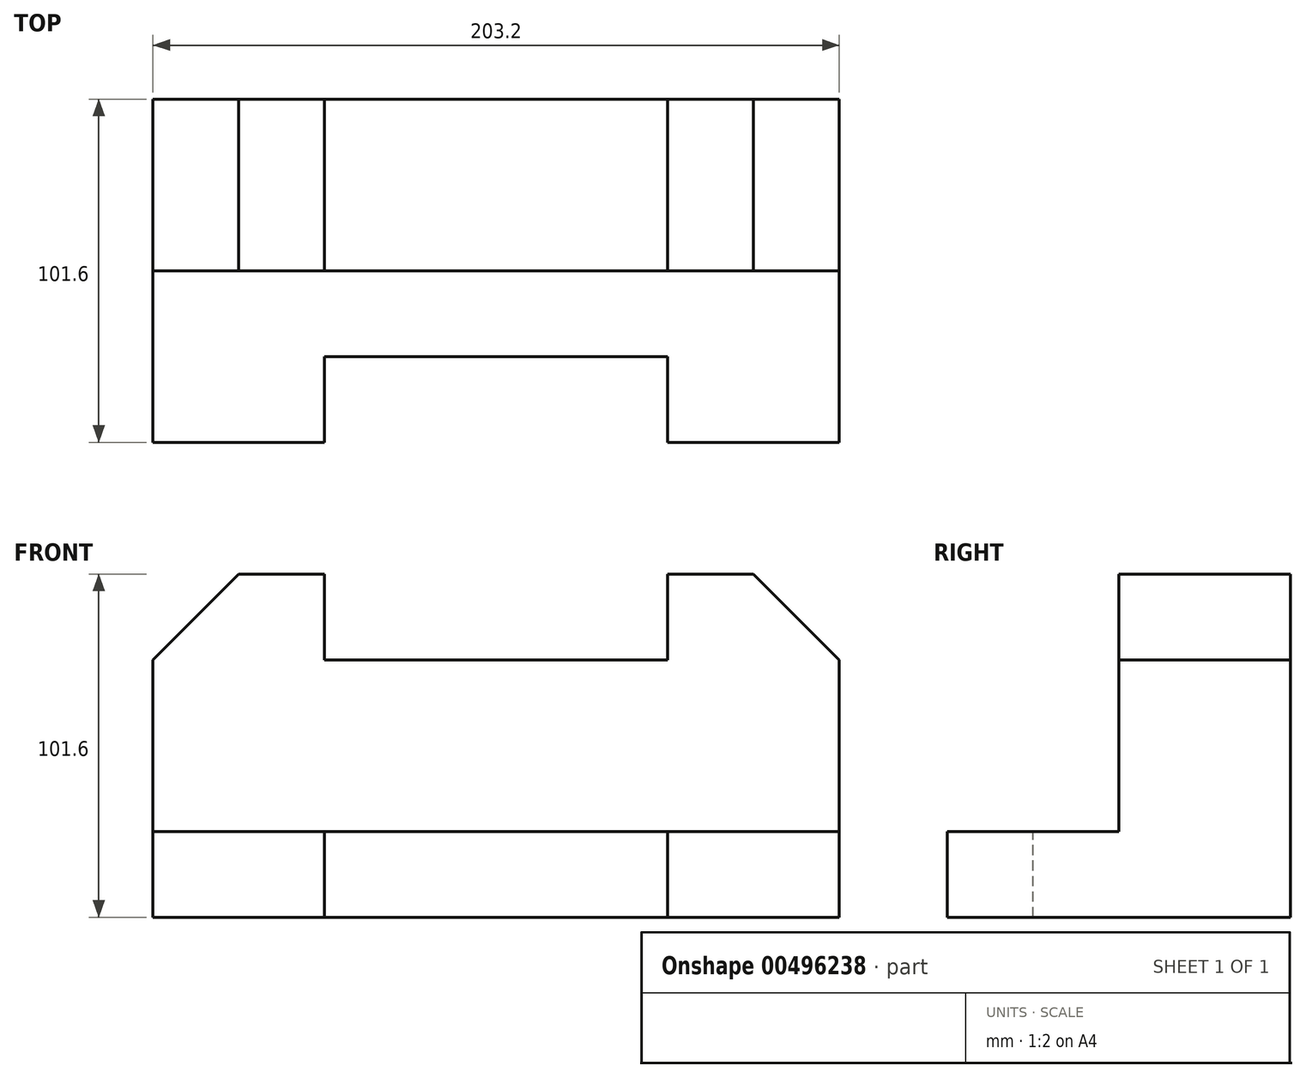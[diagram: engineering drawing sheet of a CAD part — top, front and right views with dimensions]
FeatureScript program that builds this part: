
annotation { "Feature Type Name" : "Feature", "Feature Type Description" : "" }
export const myFeature = defineFeature(function(context is Context, id is Id, definition is map)
    precondition{}
    {
        {
            var Q0;
            Q0=qCreatedBy(makeId("Front.planeOp"),FACE);
            var sketch = newSketch(context, id + "F0", { "sketchPlane" : qUnion([Q0])});
            skLineSegment(sketch, "E0.bottom", {"start": v(0, 0) * mm, "end": v(-50.8, 0) * mm});
            skLineSegment(sketch, "E0.top", {"start": v(0, 101.6) * mm, "end": v(-50.8, 101.6) * mm});
            skLineSegment(sketch, "E0.left", {"start": v(0, 0) * mm, "end": v(0, 101.6) * mm});
            skLineSegment(sketch, "E0.right", {"start": v(-50.8, 0) * mm, "end": v(-50.8, 101.6) * mm});
            skLineSegment(sketch, "E1.bottom", {"start": v(0, 0) * mm, "end": v(50.8, 0) * mm});
            skLineSegment(sketch, "E1.top", {"start": v(0, 25.4) * mm, "end": v(50.8, 25.4) * mm});
            skLineSegment(sketch, "E1.left", {"start": v(0, 0) * mm, "end": v(0, 25.4) * mm});
            skLineSegment(sketch, "E1.right", {"start": v(50.8, 0) * mm, "end": v(50.8, 25.4) * mm});
            skSolve(sketch);
        }
        {
            var Q0;
            Q0=makeQuery(id+"F0.imprint","IMPRINT",FACE,{"disambiguationData":[TD([[makeQuery(id+"F0.imprint","IMPRINT",EDGE,{"derivedFrom":sQuery(id+"F0.wireOp",EDGE,"E0.bottom")}),-1.0]])]});
            var Q1;
            Q1=makeQuery(id+"F0.imprint","IMPRINT",FACE,{"disambiguationData":[TD([[makeQuery(id+"F0.imprint","IMPRINT",EDGE,{"derivedFrom":sQuery(id+"F0.wireOp",EDGE,"E1.bottom")}),1.0]])]});
            extrude(context, id + "F1", {"entities" : qUnion([Q0, Q1]), "depth" : 203.2 * mm});
        }
        {
            var Q0;
            Q0=makeQuery(id+"F1.opExtrude","SWEPT_FACE",FACE,{"disambiguationData":[OSD([sQuery(id+"F0.wireOp",EDGE,"E1.right")])]});
            var sketch = newSketch(context, id + "F2", { "sketchPlane" : qUnion([Q0])});
            skLineSegment(sketch, "E2", {"start": v(-203.2, 0) * mm, "end": v(-152.4, 0) * mm});
            skLineSegment(sketch, "E3.bottom", {"start": v(-152.4, 0) * mm, "end": v(-50.8, 0) * mm});
            skLineSegment(sketch, "E3.top", {"start": v(-152.4, 25.4) * mm, "end": v(-50.8, 25.4) * mm});
            skLineSegment(sketch, "E3.left", {"start": v(-152.4, 0) * mm, "end": v(-152.4, 25.4) * mm});
            skLineSegment(sketch, "E3.right", {"start": v(-50.8, 0) * mm, "end": v(-50.8, 25.4) * mm});
            skSolve(sketch);
        }
        {
            var Q0;
            Q0=makeQuery(id+"F2.imprint","IMPRINT",FACE,{"disambiguationData":[TD([[makeQuery(id+"F2.imprint","IMPRINT",EDGE,{"derivedFrom":sQuery(id+"F2.wireOp",EDGE,"E3.bottom")}),1.0]])]});
            extrude(context, id + "F3", {"entities" : qUnion([Q0]), "operationType" : NewBodyOperationType.REMOVE, "oppositeDirection" : true, "depth" : 25.4 * mm});
        }
        {
            var Q0;
            Q0=makeQuery(id+"F1.opExtrude","SWEPT_FACE",FACE,{"disambiguationData":[OSD([sQuery(id+"F0.wireOp",EDGE,"E0.right")])]});
            var sketch = newSketch(context, id + "F4", { "sketchPlane" : qUnion([Q0])});
            skLineSegment(sketch, "E4", {"start": v(0, 101.6) * mm, "end": v(25.4, 101.6) * mm});
            skLineSegment(sketch, "E5", {"start": v(25.4, 101.6) * mm, "end": v(50.8, 101.6) * mm});
            skLineSegment(sketch, "E6", {"start": v(203.2, 101.6) * mm, "end": v(177.8, 101.6) * mm});
            skLineSegment(sketch, "E7", {"start": v(152.4, 101.6) * mm, "end": v(177.8, 101.6) * mm});
            skLineSegment(sketch, "E8", {"start": v(25.4, 101.6) * mm, "end": v(25.4, 76.2) * mm});
            skLineSegment(sketch, "E9", {"start": v(177.8, 101.6) * mm, "end": v(177.8, 76.2) * mm});
            skLineSegment(sketch, "E10", {"start": v(0, 101.6) * mm, "end": v(0, 76.2) * mm});
            skLineSegment(sketch, "E11", {"start": v(0, 76.2) * mm, "end": v(25.4, 101.6) * mm});
            skLineSegment(sketch, "E12", {"start": v(177.8, 101.6) * mm, "end": v(203.2, 76.2) * mm});
            skLineSegment(sketch, "E13", {"start": v(203.2, 76.2) * mm, "end": v(203.2, 101.6) * mm});
            skSolve(sketch);
        }
        {
            var Q0;
            Q0=makeQuery(id+"F4.imprint","IMPRINT",FACE,{"disambiguationData":[TD([[makeQuery(id+"F4.imprint","IMPRINT",EDGE,{"derivedFrom":sQuery(id+"F4.wireOp",EDGE,"E4")}),1.0]])]});
            var Q1;
            Q1=makeQuery(id+"F4.imprint","IMPRINT",FACE,{"disambiguationData":[TD([[makeQuery(id+"F4.imprint","IMPRINT",EDGE,{"derivedFrom":sQuery(id+"F4.wireOp",EDGE,"E6")}),1.0]])]});
            extrude(context, id + "F5", {"entities" : qUnion([Q0, Q1]), "operationType" : NewBodyOperationType.REMOVE, "oppositeDirection" : true, "depth" : 50.8 * mm});
        }
        {
            var Q0;
            Q0=makeQuery(id+"F1.opExtrude","SWEPT_FACE",FACE,{"disambiguationData":[OSD([sQuery(id+"F0.wireOp",EDGE,"E0.right")])]});
            var sketch = newSketch(context, id + "F6", { "sketchPlane" : qUnion([Q0])});
            skLineSegment(sketch, "E14", {"start": v(25.4, 101.6) * mm, "end": v(50.8, 101.6) * mm});
            skLineSegment(sketch, "E15", {"start": v(50.8, 101.6) * mm, "end": v(152.4, 101.6) * mm});
            skLineSegment(sketch, "E16", {"start": v(152.4, 101.6) * mm, "end": v(177.8, 101.6) * mm});
            skLineSegment(sketch, "E17", {"start": v(50.8, 101.6) * mm, "end": v(50.8, 76.2) * mm});
            skLineSegment(sketch, "E18", {"start": v(50.8, 76.2) * mm, "end": v(152.4, 76.2) * mm});
            skLineSegment(sketch, "E19", {"start": v(152.4, 76.2) * mm, "end": v(152.4, 101.6) * mm});
            skSolve(sketch);
        }
        {
            var Q0;
            Q0=makeQuery(id+"F6.imprint","IMPRINT",FACE,{"disambiguationData":[TD([[makeQuery(id+"F6.imprint","IMPRINT",EDGE,{"derivedFrom":sQuery(id+"F6.wireOp",EDGE,"E15")}),1.0]])]});
            extrude(context, id + "F7", {"entities" : qUnion([Q0]), "operationType" : NewBodyOperationType.REMOVE, "oppositeDirection" : true, "depth" : 50.8 * mm});
        }
        {
            var Q0;
            Q0=makeQuery(id+"F1.opExtrude","SWEPT_BODY",BODY,{"disambiguationData":[OSD([sQuery(id+"F0.wireOp",EDGE,"E0.bottom"),sQuery(id+"F0.wireOp",EDGE,"E0.top"),sQuery(id+"F0.wireOp",EDGE,"E0.left"),sQuery(id+"F0.wireOp",EDGE,"E0.right"),sQuery(id+"F0.wireOp",EDGE,"E1.bottom"),sQuery(id+"F0.wireOp",EDGE,"E1.top"),sQuery(id+"F0.wireOp",EDGE,"E1.right")])]});
            var Q1;
            Q1=makeQuery(id+"F1.opExtrude","CAP_EDGE",EDGE,{"disambiguationData":[OSD([sQuery(id+"F0.wireOp",EDGE,"E0.right")])],"isStart":false});
            transform(context, id + "F8", {"entities" : qUnion([Q0]), "transformType" : TransformType.ROTATION, "transformAxis" : qUnion([Q1]), "angle" : 270 * degree, "makeCopy" : false});
        }
    });
